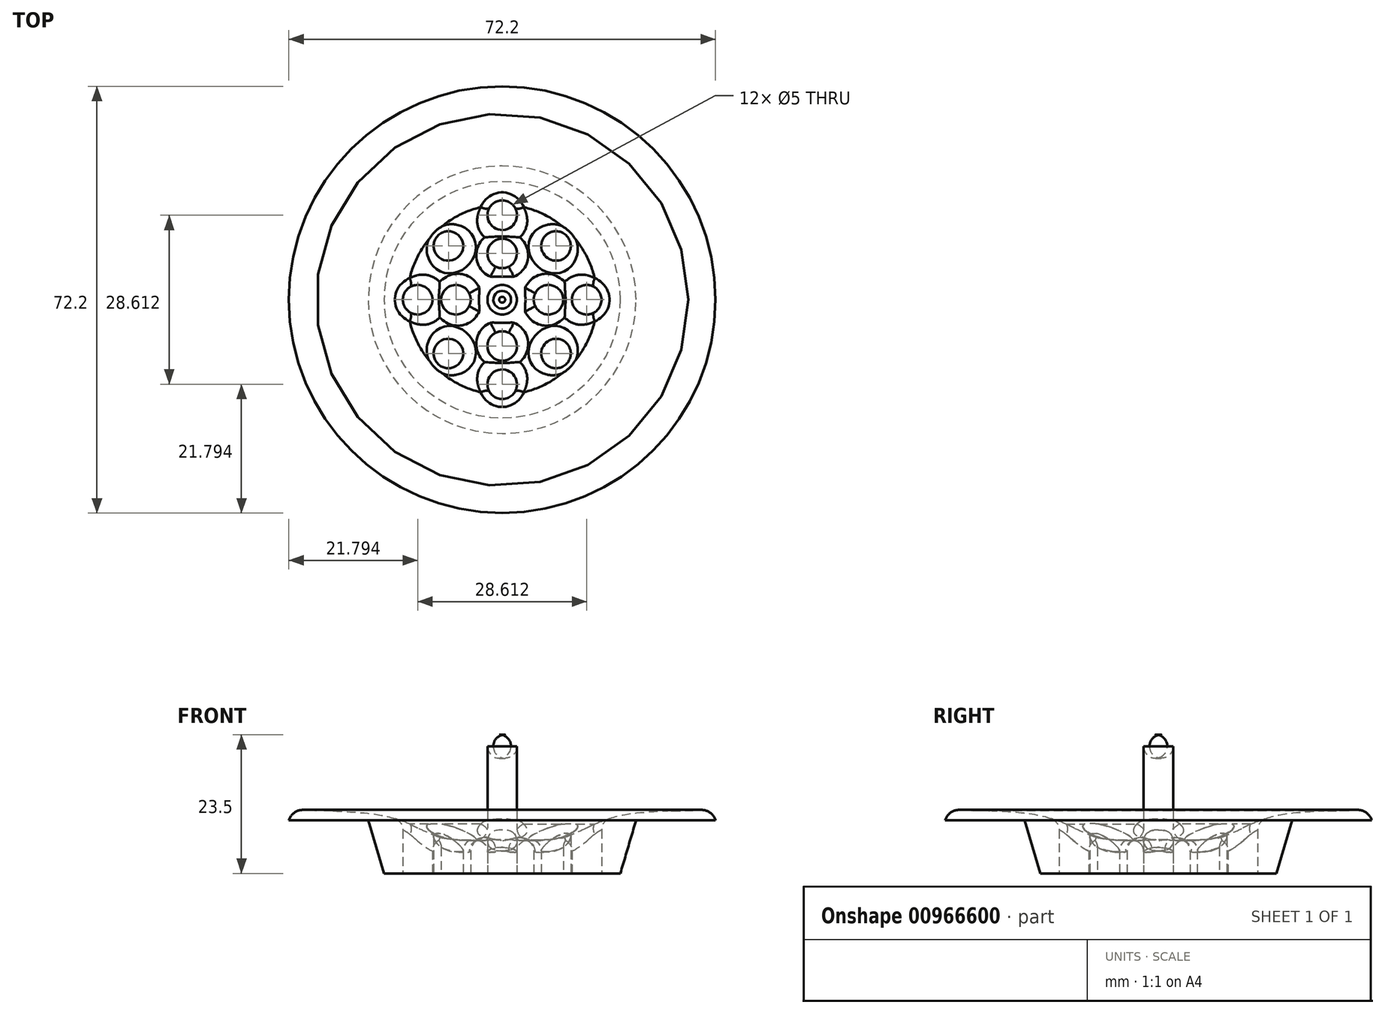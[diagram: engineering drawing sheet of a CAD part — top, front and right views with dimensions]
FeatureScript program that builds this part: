
annotation { "Feature Type Name" : "Feature", "Feature Type Description" : "" }
export const myFeature = defineFeature(function(context is Context, id is Id, definition is map)
    precondition{}
    {
        {
            var Q0;
            Q0=qCreatedBy(makeId("Front.planeOp"),FACE);
            var sketch = newSketch(context, id + "F0", { "sketchPlane" : qUnion([Q0])});
            skLineSegment(sketch, "E0", {"start": v(0, 8) * mm, "end": v(0, 0) * mm});
            skLineSegment(sketch, "E1", {"start": v(0, 0) * mm, "end": v(-20, 0) * mm});
            skLineSegment(sketch, "E2", {"start": v(-20, 0) * mm, "end": v(-22.65, 9) * mm});
            skLineSegment(sketch, "E3", {"start": v(-22.65, 9) * mm, "end": v(-36.1, 9) * mm});
            skLineSegment(sketch, "E4", {"start": v(-36.95, 11) * mm, "end": v(-36.1, 9) * mm});
            skFitSpline(sketch, "E5", {"points": [v(-36.95, 11) * mm, v(-19.34, 10.45) * mm, v(0, 8) * mm], "startDerivative": vector(60.3, -5.42) * mm, "endDerivative": vector(69.95, -0.6) * mm});
            skLineSegment(sketch, "E6", {"start": v(0, 21.23) * mm, "end": v(0, -26.38) * mm, "construction": true});
            skFitSpline(sketch, "E7", {"points": [v(0, 6.1) * mm, v(-10.57, 5.98) * mm, v(-19.34, 10.45) * mm], "startDerivative": vector(-21.5, -2.63) * mm, "endDerivative": vector(-17.15, 11.4) * mm});
            skFitSpline(sketch, "E8", {"points": [v(-14.81, 7.64) * mm, v(-20.53, 9.86) * mm, v(-31.47, 10.64) * mm, v(-31.63, 10.65) * mm], "startDerivative": vector(-10.85, 6.32) * mm, "endDerivative": vector(-1.26, 0.15) * mm});
            skSolve(sketch);
        }
        {
            var Q0;
            {var subQ0=sQuery(id+"F0.wireOp",EDGE,"E1");Q0=makeQuery(id+"F0.imprint","IMPRINT",FACE,{"disambiguationData":[TD([[makeQuery(id+"F0.imprint","IMPRINT",EDGE,{"derivedFrom":subQ0}),-1.0]])]});}
            var Q1;
            Q1=sQuery(id+"F0.wireOp",EDGE,"E0");
            revolve(context, id + "F1", {"surfaceOperationType" : NewSurfaceOperationType.NEW, "entities" : qUnion([Q0]), "axis" : qUnion([Q1]), "revolveType" : RevolveType.FULL});
        }
        {
            var Q0;
            Q0=makeQuery(id+"F1.opRevolve","SWEPT_FACE",FACE,{"disambiguationData":[OSD([sQuery(id+"F0.wireOp",EDGE,"E1")])]});
            var sketch = newSketch(context, id + "F2", { "sketchPlane" : qUnion([Q0])});
            skCircle(sketch, "E9", {"center": v(0, 0) * mm, "radius": 20.08 * mm});
            skCircle(sketch, "E10", {"center": v(0, 0) * mm, "radius": 18.2 * mm});
            skLineSegment(sketch, "E11", {"start": v(0, 18.2) * mm, "end": v(0, -18.2) * mm, "construction": true});
            skLineSegment(sketch, "E12", {"start": v(-18.2, 0) * mm, "end": v(18.2, 0) * mm, "construction": true});
            skLineSegment(sketch, "E13.bottom", {"start": v(18.2, -18.2) * mm, "end": v(-18.2, -18.2) * mm, "construction": true});
            skLineSegment(sketch, "E13.top", {"start": v(18.2, 18.2) * mm, "end": v(-18.2, 18.2) * mm, "construction": true});
            skLineSegment(sketch, "E13.left", {"start": v(18.2, -18.2) * mm, "end": v(18.2, 18.2) * mm, "construction": true});
            skLineSegment(sketch, "E13.right", {"start": v(-18.2, -18.2) * mm, "end": v(-18.2, 18.2) * mm, "construction": true});
            skLineSegment(sketch, "E14", {"start": v(-18.2, 18.2) * mm, "end": v(18.2, -18.2) * mm, "construction": true});
            skLineSegment(sketch, "E15", {"start": v(18.2, 18.2) * mm, "end": v(-18.2, -18.2) * mm, "construction": true});
            skLineSegment(sketch, "E16", {"start": v(-18.2, 0) * mm, "end": v(0, -18.2) * mm, "construction": true});
            skLineSegment(sketch, "E17", {"start": v(18.2, 0) * mm, "end": v(0, -18.2) * mm, "construction": true});
            skLineSegment(sketch, "E18", {"start": v(-18.2, 0) * mm, "end": v(0, 18.2) * mm, "construction": true});
            skLineSegment(sketch, "E19", {"start": v(18.2, 0) * mm, "end": v(0, 18.2) * mm, "construction": true});
            skCircle(sketch, "E20", {"center": v(0, 0) * mm, "radius": 7.84 * mm, "construction": true});
            skCircle(sketch, "E21", {"center": v(0, 0) * mm, "radius": 14.3 * mm, "construction": true});
            skCircle(sketch, "E22", {"center": v(-7.84, 0) * mm, "radius": 2.5 * mm});
            skCircle(sketch, "E23", {"center": v(0, 7.84) * mm, "radius": 2.5 * mm});
            skCircle(sketch, "E24", {"center": v(7.84, 0) * mm, "radius": 2.5 * mm});
            skCircle(sketch, "E25", {"center": v(0, -7.84) * mm, "radius": 2.5 * mm});
            skCircle(sketch, "E26", {"center": v(0, 0) * mm, "radius": 2.5 * mm});
            skCircle(sketch, "E27", {"center": v(-9.1, 9.1) * mm, "radius": 2.5 * mm});
            skCircle(sketch, "E28", {"center": v(9.1, 9.1) * mm, "radius": 2.5 * mm});
            skCircle(sketch, "E29", {"center": v(9.1, -9.1) * mm, "radius": 2.5 * mm});
            skCircle(sketch, "E30", {"center": v(-9.1, -9.1) * mm, "radius": 2.5 * mm});
            skCircle(sketch, "E31", {"center": v(0, -14.3) * mm, "radius": 2.5 * mm});
            skCircle(sketch, "E32", {"center": v(0, 14.3) * mm, "radius": 2.5 * mm});
            skCircle(sketch, "E33", {"center": v(-14.3, 0) * mm, "radius": 2.5 * mm});
            skCircle(sketch, "E34", {"center": v(14.3, 0) * mm, "radius": 2.5 * mm});
            skSolve(sketch);
        }
        {
            var Q0;
            Q0=makeQuery(id+"F2.imprint","IMPRINT",FACE,{"disambiguationData":[TD([[makeQuery(id+"F2.imprint","IMPRINT",EDGE,{"derivedFrom":sQuery(id+"F2.wireOp",EDGE,"E23")}),1.0]])]});
            var Q1;
            Q1=makeQuery(id+"F2.imprint","IMPRINT",FACE,{"disambiguationData":[TD([[makeQuery(id+"F2.imprint","IMPRINT",EDGE,{"derivedFrom":sQuery(id+"F2.wireOp",EDGE,"E27")}),1.0]])]});
            var Q2;
            Q2=makeQuery(id+"F2.imprint","IMPRINT",FACE,{"disambiguationData":[TD([[makeQuery(id+"F2.imprint","IMPRINT",EDGE,{"derivedFrom":sQuery(id+"F2.wireOp",EDGE,"E33")}),1.0]])]});
            var Q3;
            Q3=makeQuery(id+"F2.imprint","IMPRINT",FACE,{"disambiguationData":[TD([[makeQuery(id+"F2.imprint","IMPRINT",EDGE,{"derivedFrom":sQuery(id+"F2.wireOp",EDGE,"E22")}),1.0]])]});
            var Q4;
            Q4=makeQuery(id+"F2.imprint","IMPRINT",FACE,{"disambiguationData":[TD([[makeQuery(id+"F2.imprint","IMPRINT",EDGE,{"derivedFrom":sQuery(id+"F2.wireOp",EDGE,"E24")}),1.0]])]});
            var Q5;
            Q5=makeQuery(id+"F2.imprint","IMPRINT",FACE,{"disambiguationData":[TD([[makeQuery(id+"F2.imprint","IMPRINT",EDGE,{"derivedFrom":sQuery(id+"F2.wireOp",EDGE,"E28")}),1.0]])]});
            var Q6;
            Q6=makeQuery(id+"F2.imprint","IMPRINT",FACE,{"disambiguationData":[TD([[makeQuery(id+"F2.imprint","IMPRINT",EDGE,{"derivedFrom":sQuery(id+"F2.wireOp",EDGE,"E32")}),1.0]])]});
            var Q7;
            Q7=makeQuery(id+"F2.imprint","IMPRINT",FACE,{"disambiguationData":[TD([[makeQuery(id+"F2.imprint","IMPRINT",EDGE,{"derivedFrom":sQuery(id+"F2.wireOp",EDGE,"E34")}),1.0]])]});
            var Q8;
            Q8=makeQuery(id+"F2.imprint","IMPRINT",FACE,{"disambiguationData":[TD([[makeQuery(id+"F2.imprint","IMPRINT",EDGE,{"derivedFrom":sQuery(id+"F2.wireOp",EDGE,"E29")}),1.0]])]});
            var Q9;
            Q9=makeQuery(id+"F2.imprint","IMPRINT",FACE,{"disambiguationData":[TD([[makeQuery(id+"F2.imprint","IMPRINT",EDGE,{"derivedFrom":sQuery(id+"F2.wireOp",EDGE,"E25")}),1.0]])]});
            var Q10;
            Q10=makeQuery(id+"F2.imprint","IMPRINT",FACE,{"disambiguationData":[TD([[makeQuery(id+"F2.imprint","IMPRINT",EDGE,{"derivedFrom":sQuery(id+"F2.wireOp",EDGE,"E31")}),1.0]])]});
            var Q11;
            Q11=makeQuery(id+"F2.imprint","IMPRINT",FACE,{"disambiguationData":[TD([[makeQuery(id+"F2.imprint","IMPRINT",EDGE,{"derivedFrom":sQuery(id+"F2.wireOp",EDGE,"E30")}),1.0]])]});
            extrude(context, id + "F3", {"entities" : qUnion([Q0, Q1, Q2, Q3, Q4, Q5, Q6, Q7, Q8, Q9, Q10, Q11]), "operationType" : NewBodyOperationType.REMOVE, "oppositeDirection" : true, "depth" : 25 * mm, "offsetDistance" : 25 * mm});
        }
        {
            var Q0;
            Q0=makeQuery(id+"F1.opRevolve","SWEPT_FACE",FACE,{"disambiguationData":[OSD([sQuery(id+"F0.wireOp",EDGE,"E5")])]});
            fillet(context, id + "F4", {"entities" : qUnion([Q0]), "radius" : 2.5 * mm, "tangentPropagation" : true, "allowEdgeOverflow" : false});
        }
        {
            var Q0;
            Q0=makeQuery(id+"F2.imprint","IMPRINT",FACE,{"disambiguationData":[TD([[makeQuery(id+"F2.imprint","IMPRINT",EDGE,{"derivedFrom":sQuery(id+"F2.wireOp",EDGE,"E26")}),1.0]])]});
            extrude(context, id + "F5", {"entities" : qUnion([Q0]), "operationType" : NewBodyOperationType.ADD, "oppositeDirection" : true, "depth" : 23.5 * mm, "offsetDistance" : 25 * mm});
        }
        {
            var Q0;
            Q0=makeQuery(id+"F5.opExtrude","CAP_FACE",FACE,{"disambiguationData":[OSD([sQuery(id+"F2.wireOp",EDGE,"E26")])],"isStart":false});
            var Q1;
            Q1=makeQuery(id+"F5.boolean.opBoolean","INTERSECT",EDGE,{"derivedFrom":[makeQuery(id+"F1.opRevolve","SWEPT_FACE",FACE,{"disambiguationData":[OSD([sQuery(id+"F0.wireOp",EDGE,"E7")])]}),makeQuery(id+"F5.opExtrude","SWEPT_FACE",FACE,{"disambiguationData":[OSD([sQuery(id+"F2.wireOp",EDGE,"E26")])]})]});
            fillet(context, id + "F6", {"entities" : qUnion([Q0, Q1]), "radius" : 2 * mm, "tangentPropagation" : true, "allowEdgeOverflow" : false});
        }
        {
            var Q0;
            Q0=makeQuery(id+"F3.boolean.opBoolean","INTERSECT",EDGE,{"derivedFrom":[makeQuery(id+"F1.opRevolve","SWEPT_FACE",FACE,{"disambiguationData":[OSD([sQuery(id+"F0.wireOp",EDGE,"E7")])]}),makeQuery(id+"F3.opExtrude","SWEPT_FACE",FACE,{"disambiguationData":[OSD([sQuery(id+"F2.wireOp",EDGE,"E28")])]})]});
            var Q1;
            Q1=makeQuery(id+"F3.boolean.opBoolean","INTERSECT",EDGE,{"derivedFrom":[makeQuery(id+"F1.opRevolve","SWEPT_FACE",FACE,{"disambiguationData":[OSD([sQuery(id+"F0.wireOp",EDGE,"E7")])]}),makeQuery(id+"F3.opExtrude","SWEPT_FACE",FACE,{"disambiguationData":[OSD([sQuery(id+"F2.wireOp",EDGE,"E34")])]})]});
            var Q2;
            {var subQ0=sQuery(id+"F0.wireOp",EDGE,"E8");Q2=makeQuery(id+"F3.boolean.opBoolean","INTERSECT",EDGE,{"derivedFrom":[makeQuery(id+"F1.opRevolve","SWEPT_FACE",FACE,{"disambiguationData":[OSD([subQ0]),TDD([makeQuery(id+"F0.imprint","IMPRINT",EDGE,{"disambiguationData":[TD([[makeQuery(id+"F0.imprint","INTERSECT",VERTEX,{"disambiguationData":[OD(2.0)],"derivedFrom":[sQuery(id+"F0.wireOp",EDGE,"E5"),subQ0]}),1.0]])],"derivedFrom":subQ0})])]}),makeQuery(id+"F3.opExtrude","SWEPT_FACE",FACE,{"disambiguationData":[OSD([sQuery(id+"F2.wireOp",EDGE,"E34")])]})]});}
            var Q3;
            Q3=makeQuery(id+"F3.boolean.opBoolean","INTERSECT",EDGE,{"derivedFrom":[makeQuery(id+"F1.opRevolve","SWEPT_FACE",FACE,{"disambiguationData":[OSD([sQuery(id+"F0.wireOp",EDGE,"E7")])]}),makeQuery(id+"F3.opExtrude","SWEPT_FACE",FACE,{"disambiguationData":[OSD([sQuery(id+"F2.wireOp",EDGE,"E24")])]})]});
            var Q4;
            Q4=makeQuery(id+"F3.boolean.opBoolean","INTERSECT",EDGE,{"derivedFrom":[makeQuery(id+"F1.opRevolve","SWEPT_FACE",FACE,{"disambiguationData":[OSD([sQuery(id+"F0.wireOp",EDGE,"E7")])]}),makeQuery(id+"F3.opExtrude","SWEPT_FACE",FACE,{"disambiguationData":[OSD([sQuery(id+"F2.wireOp",EDGE,"E29")])]})]});
            var Q5;
            Q5=makeQuery(id+"F3.boolean.opBoolean","INTERSECT",EDGE,{"derivedFrom":[makeQuery(id+"F1.opRevolve","SWEPT_FACE",FACE,{"disambiguationData":[OSD([sQuery(id+"F0.wireOp",EDGE,"E7")])]}),makeQuery(id+"F3.opExtrude","SWEPT_FACE",FACE,{"disambiguationData":[OSD([sQuery(id+"F2.wireOp",EDGE,"E25")])]})]});
            var Q6;
            Q6=makeQuery(id+"F3.boolean.opBoolean","INTERSECT",EDGE,{"derivedFrom":[makeQuery(id+"F1.opRevolve","SWEPT_FACE",FACE,{"disambiguationData":[OSD([sQuery(id+"F0.wireOp",EDGE,"E7")])]}),makeQuery(id+"F3.opExtrude","SWEPT_FACE",FACE,{"disambiguationData":[OSD([sQuery(id+"F2.wireOp",EDGE,"E31")])]})]});
            var Q7;
            Q7=makeQuery(id+"F3.boolean.opBoolean","INTERSECT",EDGE,{"derivedFrom":[makeQuery(id+"F1.opRevolve","SWEPT_FACE",FACE,{"disambiguationData":[OSD([sQuery(id+"F0.wireOp",EDGE,"E7")])]}),makeQuery(id+"F3.opExtrude","SWEPT_FACE",FACE,{"disambiguationData":[OSD([sQuery(id+"F2.wireOp",EDGE,"E30")])]})]});
            var Q8;
            Q8=makeQuery(id+"F3.boolean.opBoolean","INTERSECT",EDGE,{"derivedFrom":[makeQuery(id+"F1.opRevolve","SWEPT_FACE",FACE,{"disambiguationData":[OSD([sQuery(id+"F0.wireOp",EDGE,"E7")])]}),makeQuery(id+"F3.opExtrude","SWEPT_FACE",FACE,{"disambiguationData":[OSD([sQuery(id+"F2.wireOp",EDGE,"E22")])]})]});
            var Q9;
            Q9=makeQuery(id+"F3.boolean.opBoolean","INTERSECT",EDGE,{"derivedFrom":[makeQuery(id+"F1.opRevolve","SWEPT_FACE",FACE,{"disambiguationData":[OSD([sQuery(id+"F0.wireOp",EDGE,"E7")])]}),makeQuery(id+"F3.opExtrude","SWEPT_FACE",FACE,{"disambiguationData":[OSD([sQuery(id+"F2.wireOp",EDGE,"E23")])]})]});
            var Q10;
            Q10=makeQuery(id+"F3.boolean.opBoolean","INTERSECT",EDGE,{"derivedFrom":[makeQuery(id+"F1.opRevolve","SWEPT_FACE",FACE,{"disambiguationData":[OSD([sQuery(id+"F0.wireOp",EDGE,"E7")])]}),makeQuery(id+"F3.opExtrude","SWEPT_FACE",FACE,{"disambiguationData":[OSD([sQuery(id+"F2.wireOp",EDGE,"E32")])]})]});
            var Q11;
            {var subQ0=sQuery(id+"F0.wireOp",EDGE,"E8");Q11=makeQuery(id+"F3.boolean.opBoolean","INTERSECT",EDGE,{"derivedFrom":[makeQuery(id+"F1.opRevolve","SWEPT_FACE",FACE,{"disambiguationData":[OSD([subQ0]),TDD([makeQuery(id+"F0.imprint","IMPRINT",EDGE,{"disambiguationData":[TD([[makeQuery(id+"F0.imprint","INTERSECT",VERTEX,{"disambiguationData":[OD(2.0)],"derivedFrom":[sQuery(id+"F0.wireOp",EDGE,"E5"),subQ0]}),1.0]])],"derivedFrom":subQ0})])]}),makeQuery(id+"F3.opExtrude","SWEPT_FACE",FACE,{"disambiguationData":[OSD([sQuery(id+"F2.wireOp",EDGE,"E32")])]})]});}
            var Q12;
            Q12=makeQuery(id+"F3.boolean.opBoolean","INTERSECT",EDGE,{"derivedFrom":[makeQuery(id+"F1.opRevolve","SWEPT_FACE",FACE,{"disambiguationData":[OSD([sQuery(id+"F0.wireOp",EDGE,"E7")])]}),makeQuery(id+"F3.opExtrude","SWEPT_FACE",FACE,{"disambiguationData":[OSD([sQuery(id+"F2.wireOp",EDGE,"E27")])]})]});
            var Q13;
            Q13=makeQuery(id+"F3.boolean.opBoolean","INTERSECT",EDGE,{"derivedFrom":[makeQuery(id+"F1.opRevolve","SWEPT_FACE",FACE,{"disambiguationData":[OSD([sQuery(id+"F0.wireOp",EDGE,"E7")])]}),makeQuery(id+"F3.opExtrude","SWEPT_FACE",FACE,{"disambiguationData":[OSD([sQuery(id+"F2.wireOp",EDGE,"E33")])]})]});
            var Q14;
            {var subQ0=sQuery(id+"F0.wireOp",EDGE,"E8");Q14=makeQuery(id+"F3.boolean.opBoolean","INTERSECT",EDGE,{"derivedFrom":[makeQuery(id+"F1.opRevolve","SWEPT_FACE",FACE,{"disambiguationData":[OSD([subQ0]),TDD([makeQuery(id+"F0.imprint","IMPRINT",EDGE,{"disambiguationData":[TD([[makeQuery(id+"F0.imprint","INTERSECT",VERTEX,{"disambiguationData":[OD(2.0)],"derivedFrom":[sQuery(id+"F0.wireOp",EDGE,"E5"),subQ0]}),1.0]])],"derivedFrom":subQ0})])]}),makeQuery(id+"F3.opExtrude","SWEPT_FACE",FACE,{"disambiguationData":[OSD([sQuery(id+"F2.wireOp",EDGE,"E33")])]})]});}
            var Q15;
            {var subQ0=sQuery(id+"F0.wireOp",EDGE,"E8");Q15=makeQuery(id+"F3.boolean.opBoolean","INTERSECT",EDGE,{"derivedFrom":[makeQuery(id+"F1.opRevolve","SWEPT_FACE",FACE,{"disambiguationData":[OSD([subQ0]),TDD([makeQuery(id+"F0.imprint","IMPRINT",EDGE,{"disambiguationData":[TD([[makeQuery(id+"F0.imprint","INTERSECT",VERTEX,{"disambiguationData":[OD(2.0)],"derivedFrom":[sQuery(id+"F0.wireOp",EDGE,"E5"),subQ0]}),1.0]])],"derivedFrom":subQ0})])]}),makeQuery(id+"F3.opExtrude","SWEPT_FACE",FACE,{"disambiguationData":[OSD([sQuery(id+"F2.wireOp",EDGE,"E31")])]})]});}
            fillet(context, id + "F7", {"entities" : qUnion([Q0, Q1, Q2, Q3, Q4, Q5, Q6, Q7, Q8, Q9, Q10, Q11, Q12, Q13, Q14, Q15]), "radius" : 2 * mm, "tangentPropagation" : true, "allowEdgeOverflow" : false});
        }
    });
